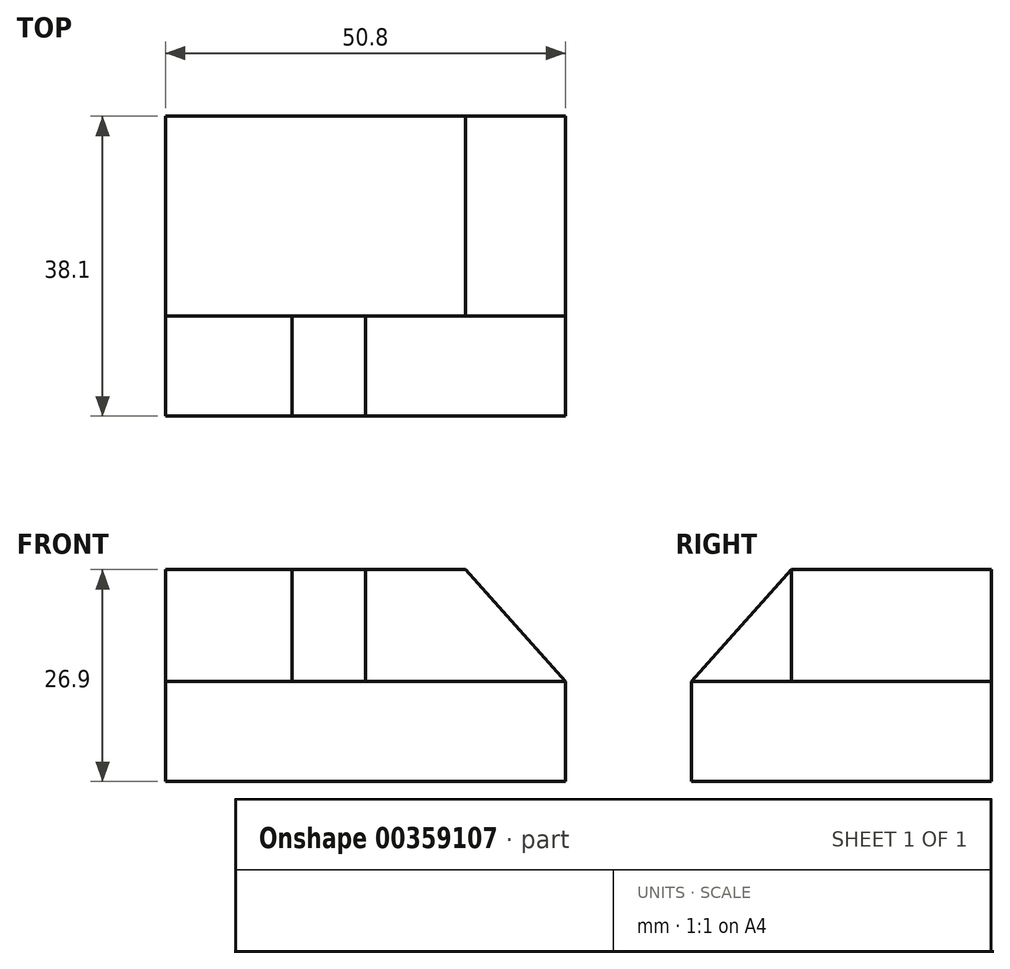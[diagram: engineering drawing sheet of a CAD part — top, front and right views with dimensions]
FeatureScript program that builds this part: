
annotation { "Feature Type Name" : "Feature", "Feature Type Description" : "" }
export const myFeature = defineFeature(function(context is Context, id is Id, definition is map)
    precondition{}
    {
        {
            var Q0;
            Q0=qCreatedBy(makeId("Front.planeOp"),FACE);
            var sketch = newSketch(context, id + "F0", { "sketchPlane" : qUnion([Q0])});
            skLineSegment(sketch, "E0", {"start": v(-66.84, 3.26) * mm, "end": v(-66.84, 30.16) * mm});
            skLineSegment(sketch, "E1", {"start": v(-66.84, 30.16) * mm, "end": v(-28.74, 30.16) * mm});
            skLineSegment(sketch, "E2", {"start": v(-28.74, 30.16) * mm, "end": v(-16.04, 15.96) * mm});
            skLineSegment(sketch, "E3", {"start": v(-16.04, 15.96) * mm, "end": v(-16.04, 3.26) * mm});
            skLineSegment(sketch, "E4", {"start": v(-16.04, 3.26) * mm, "end": v(-66.84, 3.26) * mm});
            skSolve(sketch);
        }
        {
            var Q0;
            Q0 = qSketchRegion(id + "F0", true);
            extrude(context, id + "F1", {"entities" : qUnion([Q0]), "depth" : 25.4 * mm});
        }
        {
            var Q0;
            Q0=makeQuery(id+"F1.opExtrude","CAP_FACE",FACE,{"disambiguationData":[OSD([sQuery(id+"F0.wireOp",EDGE,"E0"),sQuery(id+"F0.wireOp",EDGE,"E1"),sQuery(id+"F0.wireOp",EDGE,"E2"),sQuery(id+"F0.wireOp",EDGE,"E3"),sQuery(id+"F0.wireOp",EDGE,"E4")])],"isStart":false});
            var sketch = newSketch(context, id + "F2", { "sketchPlane" : qUnion([Q0])});
            skLineSegment(sketch, "E5", {"start": v(-16.04, 15.96) * mm, "end": v(-66.84, 15.96) * mm});
            skSolve(sketch);
        }
        {
            var Q0;
            Q0 = qSketchRegion(id + "F2", true);
            var Q1;
            {var subQ0=sQuery(id+"F2.wireOp",EDGE,"E5");Q1=makeQuery(id+"F2.imprint","IMPRINT",FACE,{"disambiguationData":[TD([[makeQuery(id+"F2.imprint","IMPRINT",EDGE,{"derivedFrom":subQ0}),1.0]])]});}
            extrude(context, id + "F3", {"entities" : qUnion([Q0, Q1]), "operationType" : NewBodyOperationType.ADD, "depth" : 12.7 * mm});
        }
        {
            var Q0;
            Q0=makeQuery(id+"F1.opExtrude","CAP_FACE",FACE,{"disambiguationData":[OSD([sQuery(id+"F0.wireOp",EDGE,"E0"),sQuery(id+"F0.wireOp",EDGE,"E1"),sQuery(id+"F0.wireOp",EDGE,"E2"),sQuery(id+"F0.wireOp",EDGE,"E3"),sQuery(id+"F0.wireOp",EDGE,"E4")])],"isStart":false});
            var sketch = newSketch(context, id + "F4", { "sketchPlane" : qUnion([Q0])});
            skLineSegment(sketch, "E6", {"start": v(-50.77, 30.16) * mm, "end": v(-50.77, 15.96) * mm});
            skLineSegment(sketch, "E7", {"start": v(-50.77, 15.96) * mm, "end": v(-41.44, 15.96) * mm});
            skLineSegment(sketch, "E8", {"start": v(-41.44, 15.96) * mm, "end": v(-41.44, 30.16) * mm});
            skLineSegment(sketch, "E9", {"start": v(-41.44, 30.16) * mm, "end": v(-50.77, 30.16) * mm});
            skSolve(sketch);
        }
        {
            var Q0;
            Q0 = qSketchRegion(id + "F4", true);
            var Q1;
            Q1 = qSketchRegion(id + "F6", true);
            extrude(context, id + "F5", {"entities" : qUnion([Q0, Q1]), "operationType" : NewBodyOperationType.ADD, "depth" : 12.7 * mm});
        }
        {
            var Q0;
            Q0=makeQuery(id+"F5.opExtrude","SWEPT_FACE",FACE,{"disambiguationData":[OSD([sQuery(id+"F4.wireOp",EDGE,"E8")])]});
            var sketch = newSketch(context, id + "F6", { "sketchPlane" : qUnion([Q0])});
            skLineSegment(sketch, "E10", {"start": v(-25.4, 30.16) * mm, "end": v(-38.1, 15.96) * mm});
            skSolve(sketch);
        }
        {
            var Q0;
            Q0 = qSketchRegion(id + "F6", true);
            var Q1;
            Q1=makeQuery(id+"F6.imprint","IMPRINT",FACE,{"disambiguationData":[TD([[makeQuery(id+"F6.imprint","IMPRINT",EDGE,{"derivedFrom":sQuery(id+"F6.wireOp",EDGE,"E10")}),-1.0]])]});
            extrude(context, id + "F7", {"entities" : qUnion([Q0, Q1]), "operationType" : NewBodyOperationType.REMOVE, "oppositeDirection" : true, "depth" : 25.4 * mm});
        }
    });
